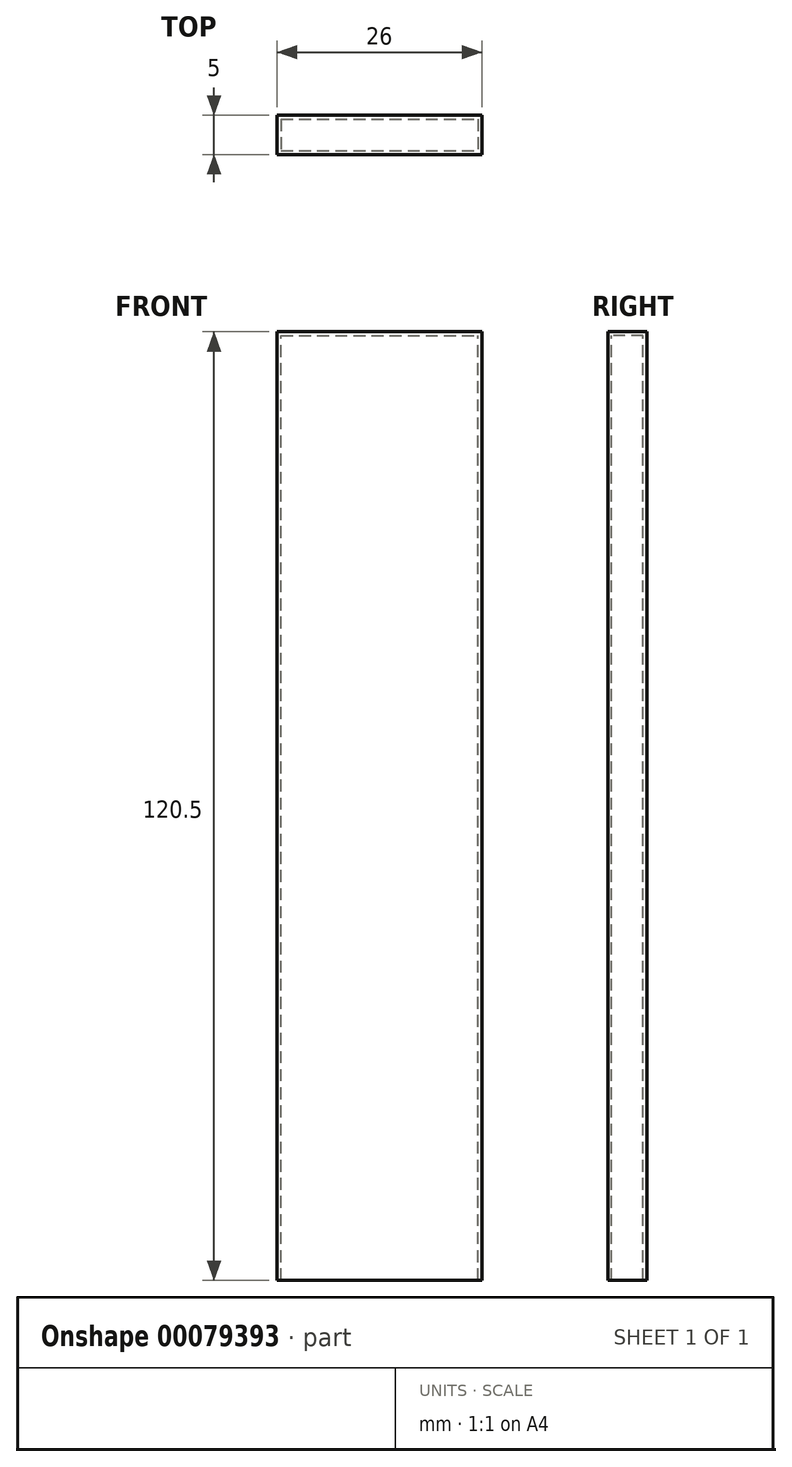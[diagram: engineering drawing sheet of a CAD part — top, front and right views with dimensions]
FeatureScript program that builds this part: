
annotation { "Feature Type Name" : "Feature", "Feature Type Description" : "" }
export const myFeature = defineFeature(function(context is Context, id is Id, definition is map)
    precondition{}
    {
        {
            var Q0;
            Q0=qCreatedBy(makeId("Top.planeOp"),FACE);
            var sketch = newSketch(context, id + "F0", { "sketchPlane" : qUnion([Q0])});
            skLineSegment(sketch, "E0.bottom", {"start": v(-12.5, 2) * mm, "end": v(12.5, 2) * mm});
            skLineSegment(sketch, "E0.top", {"start": v(-12.5, -2) * mm, "end": v(12.5, -2) * mm});
            skLineSegment(sketch, "E0.left", {"start": v(-12.5, 2) * mm, "end": v(-12.5, -2) * mm});
            skLineSegment(sketch, "E0.right", {"start": v(12.5, 2) * mm, "end": v(12.5, -2) * mm});
            skPoint(sketch, "E0.middle", {"position": v(0, 0) * mm});
            skLineSegment(sketch, "E1.0", {"start": v(-13, -2.5) * mm, "end": v(13, -2.5) * mm});
            skLineSegment(sketch, "E1.1", {"start": v(-13, 2.5) * mm, "end": v(-13, -2.5) * mm});
            skLineSegment(sketch, "E1.2", {"start": v(-13, 2.5) * mm, "end": v(13, 2.5) * mm});
            skLineSegment(sketch, "E1.3", {"start": v(13, 2.5) * mm, "end": v(13, -2.5) * mm});
            skSolve(sketch);
        }
        {
            var Q0;
            Q0=makeQuery(id+"F0.imprint","IMPRINT",FACE,{"disambiguationData":[TD([[makeQuery(id+"F0.imprint","IMPRINT",EDGE,{"derivedFrom":sQuery(id+"F0.wireOp",EDGE,"E0.bottom")}),1.0]])]});
            var Q1;
            Q1=makeQuery(id+"F0.imprint","IMPRINT",FACE,{"disambiguationData":[TD([[makeQuery(id+"F0.imprint","IMPRINT",EDGE,{"derivedFrom":sQuery(id+"F0.wireOp",EDGE,"E0.bottom")}),-1.0]])]});
            extrude(context, id + "F1", {"entities" : qUnion([Q0, Q1]), "depth" : 0.5 * mm});
        }
        {
            var Q0;
            Q0=makeQuery(id+"F0.imprint","IMPRINT",FACE,{"disambiguationData":[TD([[makeQuery(id+"F0.imprint","IMPRINT",EDGE,{"derivedFrom":sQuery(id+"F0.wireOp",EDGE,"E0.bottom")}),1.0]])]});
            extrude(context, id + "F2", {"entities" : qUnion([Q0]), "operationType" : NewBodyOperationType.ADD, "oppositeDirection" : true, "depth" : 120 * mm});
        }
    });
